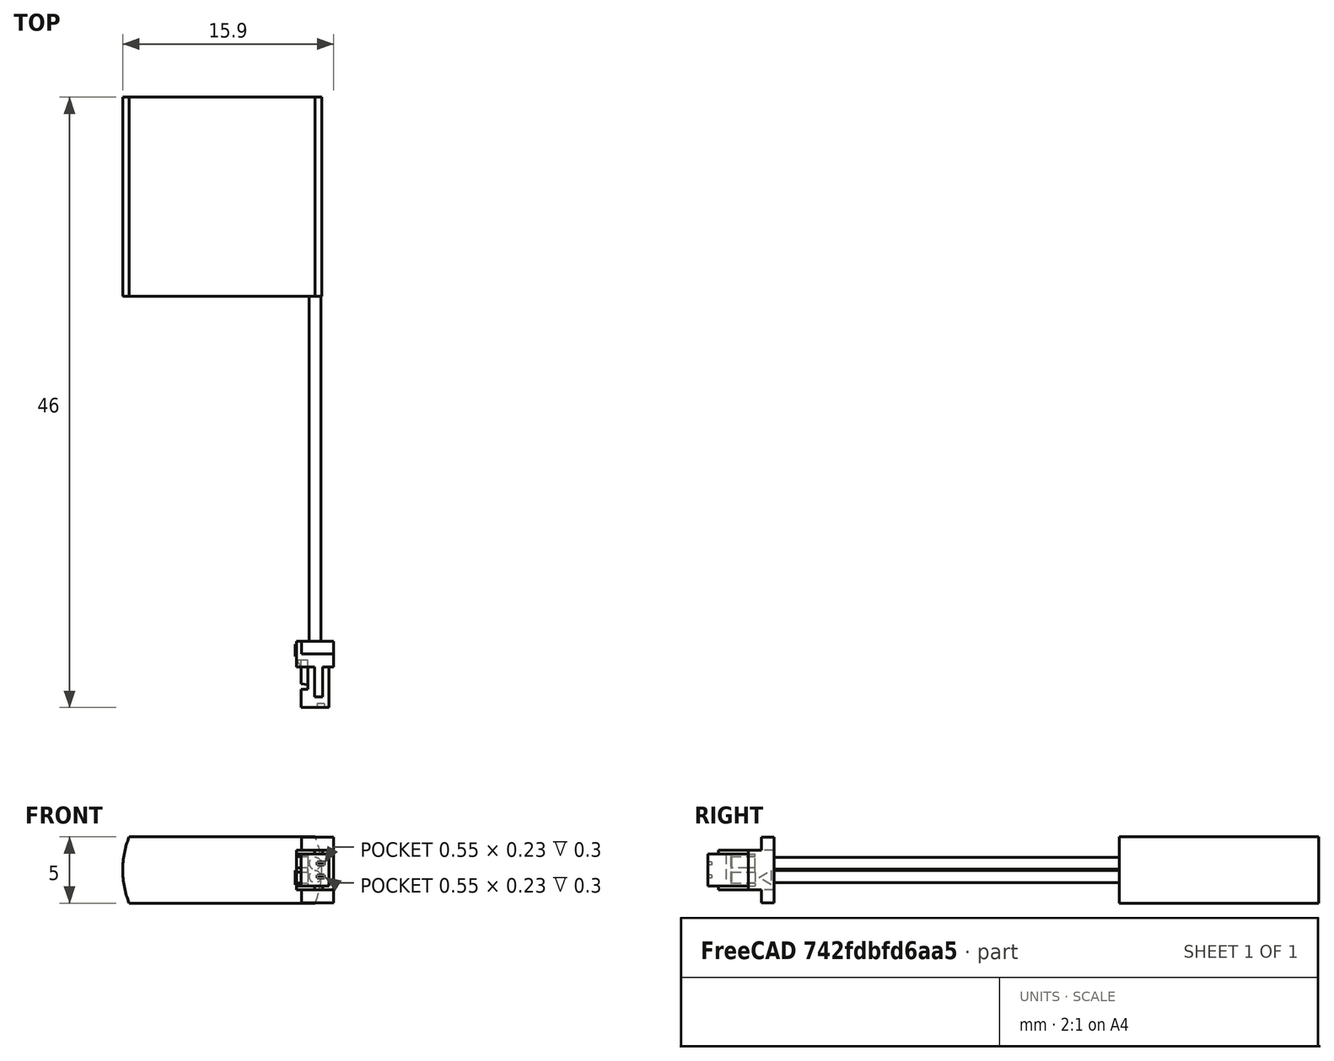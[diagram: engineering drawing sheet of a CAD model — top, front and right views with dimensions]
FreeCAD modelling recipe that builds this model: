
FCSTD DOCUMENT  (FreeCAD 2021.519R24301 +3652 (Git))
Label: ASR00011_70mAh
License: Other
objects: TechDraw::DrawViewDimension×4, Sketcher::SketchObject×3, PartDesign::Pad×3, TechDraw::DrawViewPart×2, TechDraw::DrawViewAnnotation×2, PartDesign::Pocket×1, PartDesign::Mirrored×1, PartDesign::Body×1, Part::Feature×1, Part::MultiFuse×1, TechDraw::DrawSVGTemplate×1, TechDraw::DrawPage×1, Mesh::Feature×1
note: 21 computed .brp shape members not serialized (recipe doc carries the construction recipe); baked Part::Feature solids carry a one-line shape summary decoded from their .brp

FEATURE [Sketcher::SketchObject] Sketch
  FullyConstrained = true
  MapMode = 5
  Support = -> [XY_Plane]
  sketch-geometry (4):
    g0: LineSegment StartX=-7.5 StartY=7.5 StartZ=0 EndX=7.5 EndY=7.5 EndZ=0
    g1: LineSegment StartX=7.5 StartY=7.5 StartZ=0 EndX=7.5 EndY=-7.5 EndZ=0
    g2: LineSegment StartX=7.5 StartY=-7.5 StartZ=0 EndX=-7.5 EndY=-7.5 EndZ=0
    g3: LineSegment StartX=-7.5 StartY=-7.5 StartZ=0 EndX=-7.5 EndY=7.5 EndZ=0
  constraints (10):
    c: Coincident(g0,g1)
    c: Coincident(g1,g2)
    c: Coincident(g2,g3)
    c: Coincident(g3,g0)
    c: Horizontal(g2)
    c: Vertical(g1)
    c: Symmetric(g0,g2,g-1)
    c: Symmetric(g0,g0,g-2)
    c: DistanceX(g0,g0) = 15
    c: DistanceY(g3,g3) = 15
FEATURE [PartDesign::Pad] Pad
  ClaimChildren = false
  Direction = (1,1,1)
  Fit = 0
  FitJoin = 0
  InnerFit = 0
  InnerFitJoin = 0
  InnerTaperAngle = 0
  InnerTaperAngleRev = 0
  Length = 5
  Length2 = 100
  Midplane = true
  NewSolid = false
  Profile = -> Sketch
  Suppress = false
  Type = 0
FEATURE [Sketcher::SketchObject] Sketch001
  ExternalGeometry = -> [Pad]
  FullyConstrained = true
  MapMode = 5
  Placement = pos=(0,7.5,0) rot=(0,0.707107,0.707107;3.14159rad)
  Support = -> [Pad]
  sketch-geometry (5):
    g0: ArcOfCircle CenterX=-1 CenterY=-5e-16 CenterZ=0 NormalX=0 NormalY=0 NormalZ=1 AngleXU=0 Radius=6.5 StartAngle=2.7468 EndAngle=3.53638
    g1: LineSegment [constr] StartX=-7 StartY=-2.5 StartZ=0 EndX=-7 EndY=2.5 EndZ=0
    g2: LineSegment StartX=-7 StartY=-2.5 StartZ=0 EndX=-8.5 EndY=-2.5 EndZ=0
    g3: LineSegment StartX=-7 StartY=2.5 StartZ=0 EndX=-8.5 EndY=2.5 EndZ=0
    g4: LineSegment StartX=-8.5 StartY=2.5 StartZ=0 EndX=-8.5 EndY=-2.5 EndZ=0
  constraints (15):
    c: PointOnObject(g0,g-5)
    c: PointOnObject(g0,g-4)
    c: Tangent(g0,g-3)
    c: Coincident(g1,g0)
    c: Coincident(g1,g0)
    c: Vertical(g1)
    c: Coincident(g2,g0)
    c: Horizontal(g2)
    c: Coincident(g3,g0)
    c: Horizontal(g3)
    c: Coincident(g4,g3)
    c: Coincident(g4,g2)
    c: Vertical(g4)
    c: DistanceX(g3,g-4) = 1
    c: DistanceX(g-4,g0) = 0.5
FEATURE [PartDesign::Pocket] Pocket
  BaseFeature = -> Pad
  ClaimChildren = false
  Fit = 0
  FitJoin = 0
  InnerFit = 0
  InnerFitJoin = 0
  InnerTaperAngle = 0
  InnerTaperAngleRev = 0
  Length = 5
  Length2 = 100
  NewSolid = false
  Profile = -> Sketch001
  Suppress = false
  Type = 1
FEATURE [PartDesign::Mirrored] Mirrored
  BaseFeature = -> Pocket
  CopyShape = true
  MirrorPlane = -> Sketch001 [V_Axis]
  NewSolid = false
  OriginalSubs = -> [Pocket]
  Originals = -> [Pocket]
  ParallelTransform = true
  SubTransform = true
  Suppress = false
FEATURE [PartDesign::Pad] Pad001
  BaseFeature = -> Mirrored
  ClaimChildren = false
  Direction = (1,1,1)
  Fit = 0
  FitJoin = 0
  InnerFit = 0
  InnerFitJoin = 0
  InnerTaperAngle = 0
  InnerTaperAngleRev = 0
  Length = 7.85
  Length2 = 100
  NewSolid = false
  Profile = -> Mirrored [Face8]
  Reversed = true
  Suppress = false
  Type = 0
FEATURE [Sketcher::SketchObject] Sketch002
  ExternalGeometry = -> [Pad001]
  FullyConstrained = true
  MapMode = 5
  Placement = pos=(0,-7.5,0) rot=(1,0,0;1.5708rad)
  Support = -> [Pad001]
  sketch-geometry (6):
    g0: Circle CenterX=7 CenterY=0.5 CenterZ=0 NormalX=0 NormalY=0 NormalZ=1 AngleXU=0 Radius=0.45
    g1: Circle CenterX=7 CenterY=-0.5 CenterZ=0 NormalX=0 NormalY=0 NormalZ=1 AngleXU=0 Radius=0.45
    g2: LineSegment [constr] StartX=7 StartY=-0.5 StartZ=0 EndX=7 EndY=0.5 EndZ=0
    g3: GeomPoint [constr] X=7 Y=0.05 Z=0
    g4: GeomPoint [constr] X=7 Y=-0.05 Z=0
    g5: LineSegment [constr] StartX=7 StartY=0.5 StartZ=0 EndX=7.45 EndY=0.5 EndZ=0
  constraints (13):
    c: Coincident(g2,g1)
    c: Coincident(g2,g0)
    c: Equal(g0,g1)
    c: Diameter(g0) = 0.9
    c: Symmetric(g0,g1,g-1)
    c: PointOnObject(g3,g2)
    c: PointOnObject(g4,g1)
    c: Symmetric(g3,g4,g-1)
    c: DistanceY(g-3,g3) = 0.05
    c: Coincident(g5,g0)
    c: PointOnObject(g5,g0)
    c: Horizontal(g5)
    c: DistanceX(g5,g-3) = 0.05
FEATURE [PartDesign::Pad] Pad002
  BaseFeature = -> Pad001
  ClaimChildren = false
  Direction = (1,1,1)
  Fit = 0
  FitJoin = 0
  InnerFit = 0
  InnerFitJoin = 0
  InnerTaperAngle = 0
  InnerTaperAngleRev = 0
  Length = 26
  Length2 = 100
  NewSolid = false
  Profile = -> Sketch002
  Suppress = false
  Type = 0
FEATURE [PartDesign::Body] Body
  AutoGroupSolids = false
  ExportMode = 0
  Group = -> [Sketch,Pad,Sketch001,Pocket,Mirrored,Pad001,Sketch002,Pad002]
  Origin = -> Origin
  Tip = -> Pad002
  _ExportChildren = -> [Pad,Pocket,Mirrored,Pad001,Pad002]
  _GroupVersion = 1
FEATURE [Part::Feature] Solid  label="Body007"
  Placement = pos=(5.71545,-35.5,7.3e-15) rot=(0,0,1;0rad)
  shape: bbox 2.9 x 5 x 4.94 mm, 60 faces (baked)
FEATURE [Part::MultiFuse] Fusion
  Shapes = -> [Body,Solid]
FEATURE [TechDraw::DrawSVGTemplate] Template
  Height = 210
  Orientation = 1
  Width = 297
FEATURE [TechDraw::DrawViewPart] View
  CoarseView = false
  Direction = (0,0,1)
  Focus = 100
  HardHidden = false
  IsoCount = 0
  IsoHidden = false
  IsoVisible = false
  LockPosition = false
  Perspective = false
  Rotation = 180
  Scale = 2.38
  ScaleType = 0
  SeamHidden = false
  SeamVisible = true
  SmoothHidden = false
  SmoothVisible = true
  Source = -> [Fusion]
  X = 178.5
  XDirection = (1,0,0)
  Y = 105
FEATURE [TechDraw::DrawViewPart] View001
  CoarseView = false
  Direction = (-1,0,0)
  Focus = 100
  HardHidden = false
  IsoCount = 0
  IsoHidden = false
  IsoVisible = false
  LockPosition = false
  Perspective = false
  Rotation = 90
  Scale = 2.38
  ScaleType = 0
  SeamHidden = false
  SeamVisible = true
  SmoothHidden = false
  SmoothVisible = true
  Source = -> [Fusion]
  X = 118.5
  XDirection = (0,-1,0)
  Y = 105
FEATURE [TechDraw::DrawViewAnnotation] Annotation
  Font = MS Shell Dlg 2
  LineSpace = 80
  LockPosition = false
  MaxWidth = -1
  Rotation = 0
  ScaleType = 0
  Text = SIDE VIEW
  TextSize = 6
  TextStyle = 0
  X = 118.5
  Y = 162
FEATURE [TechDraw::DrawViewAnnotation] Annotation001
  Font = MS Shell Dlg 2
  LineSpace = 80
  LockPosition = false
  MaxWidth = -1
  Rotation = 0
  ScaleType = 0
  Text = TOP VIEW
  TextSize = 6
  TextStyle = 0
  X = 178.5
  Y = 162
FEATURE [TechDraw::DrawViewDimension] Dimension
  Arbitrary = false
  ArbitraryTolerances = false
  EqualTolerance = true
  FormatSpec = %.1f
  FormatSpecOverTolerance = %+.1f
  FormatSpecUnderTolerance = %+.1f
  Inverted = false
  LockPosition = false
  MeasureType = 1
  OverTolerance = 0.5
  References2D = -> [View001]
  Rotation = 0
  ScaleType = 0
  TheoreticalExact = false
  Type = 1
  UnderTolerance = -0.5
  X = -34
  Y = -59
FEATURE [TechDraw::DrawViewDimension] Dimension001
  Arbitrary = false
  ArbitraryTolerances = false
  EqualTolerance = true
  FormatSpec = %.1f
  FormatSpecOverTolerance = %+.1f
  FormatSpecUnderTolerance = %+.1f
  Inverted = false
  LockPosition = false
  MeasureType = 1
  OverTolerance = 2
  References2D = -> [View]
  Rotation = 0
  ScaleType = 0
  TheoreticalExact = false
  Type = 1
  UnderTolerance = -2
  X = 36.071
  Y = -59
FEATURE [TechDraw::DrawViewDimension] Dimension002
  Arbitrary = false
  ArbitraryTolerances = false
  EqualTolerance = true
  FormatSpec = %.1f
  FormatSpecOverTolerance = %+.1f
  FormatSpecUnderTolerance = %+.1f
  Inverted = false
  LockPosition = false
  MeasureType = 1
  OverTolerance = 3
  References2D = -> [View]
  Rotation = 0
  ScaleType = 0
  TheoreticalExact = false
  Type = 2
  UnderTolerance = -3
  X = -34
  Y = -35.8
FEATURE [TechDraw::DrawViewDimension] Dimension003
  Arbitrary = false
  ArbitraryTolerances = false
  EqualTolerance = true
  FormatSpec = %.1f
  FormatSpecOverTolerance = %+.1f
  FormatSpecUnderTolerance = %+.1f
  Inverted = false
  LockPosition = false
  MeasureType = 1
  OverTolerance = 5
  References2D = -> [View]
  Rotation = 0
  ScaleType = 0
  TheoreticalExact = false
  Type = 2
  UnderTolerance = -5
  X = -34
  Y = 11.9
FEATURE [TechDraw::DrawPage] Page
  KeepUpdated = true
  NextBalloonIndex = 1
  ProjectionType = 0
  Template = -> Template
  Views = -> [View,View001,Annotation,Annotation001,Dimension,Dimension001,Dimension002,Dimension003]
FEATURE [Mesh::Feature] Mesh  label="Fusion (Meshed)"
